# Revit family: HL_Универсальный трап вертикальный_HL73Pr
name_source: partatom
category: Instalační zařizovací předměty
revit_build: Autodesk Revit 2016 (Build: 20151007_0715(x64)
units: mm (PartAtom-declared; Revit-internal decimal feet)

## family parameters
Bod výpočtu místnosti = Ano
Kóta kulaté spojky = Použít průměr
Nadpis OmniClass = Deck Waste Water Drains
Ořezat dutým tvarem při načtení = Ne
Sdílené = Ne
Typ součásti = Normální
Vždy vertikální = Ano
Založené na pracovní rovině = Ne
Číslo OmniClass = 23.70.50.21.24.14

## types (1)
- HL_Универсальный трап вертикальный_HL73Pr
    Cena = 0 $
    EAN = 9003076032327
    Klíčová poznámka = HL73Pr
    Komentáře k typům = Универсальный трап вертикальный DN110 
с "сухим" сифоном
    Model = HL73Pr
    Popis = Трап для внутренних помещений
    URL = http://www.hutterer-lechner.com
    Výrobce = HL Hutterer & Lechner GmbH
    ВЕС = 0,457 kg
    МАКСИМАЛЬНАЯ НАГРУЗКА КЛАССА = K3 - 300 kg
    МАТЕРИАЛ = PP / Edelstahl V2A
    НАСАДКА = 121x121mm
    НОМИНАЛЬНЫЙ ДИАМЕТР = 110 mm
    ПРОИЗВОДИТЕЛЬНОСТЬ = 0,46 l/s
    РАЗМЕР = DN110
    РЕШЁТКА = 115x115mm/ V2A
